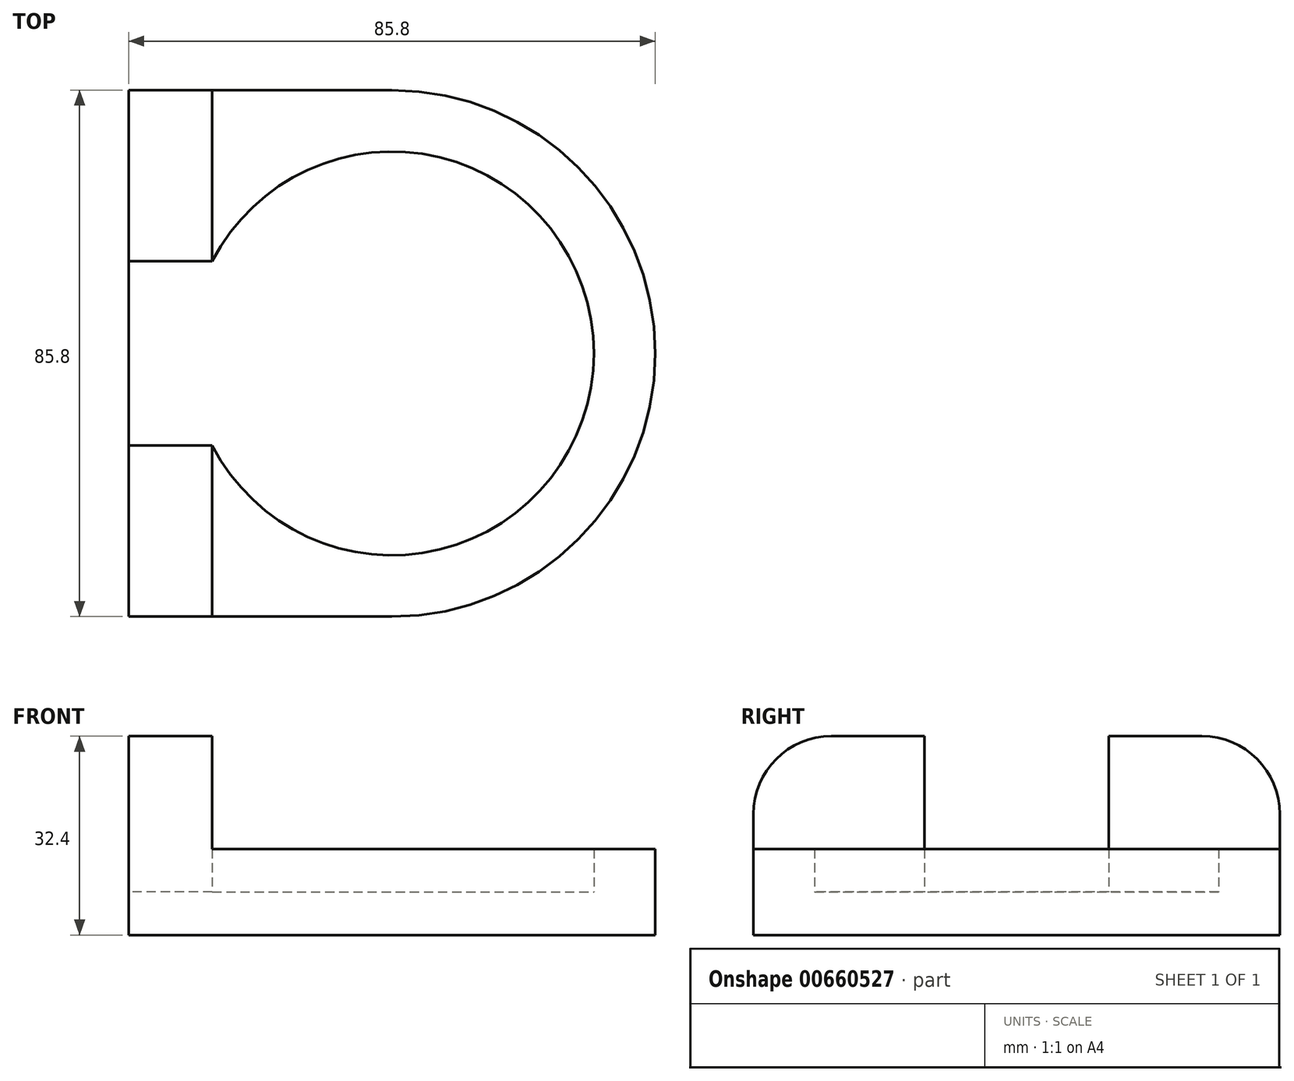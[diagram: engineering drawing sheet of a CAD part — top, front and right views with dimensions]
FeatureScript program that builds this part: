
annotation { "Feature Type Name" : "Feature", "Feature Type Description" : "" }
export const myFeature = defineFeature(function(context is Context, id is Id, definition is map)
    precondition{}
    {
        {
            var Q0;
            Q0=qCreatedBy(makeId("Top.planeOp"),FACE);
            var sketch = newSketch(context, id + "F0", { "sketchPlane" : qUnion([Q0])});
            skCircle(sketch, "E0", {"center": v(0, 0) * mm, "radius": 32.9 * mm});
            skCircle(sketch, "E1", {"center": v(0, 0) * mm, "radius": 42.9 * mm});
            skLineSegment(sketch, "E2", {"start": v(0, 42.9) * mm, "end": v(-42.9, 42.9) * mm});
            skLineSegment(sketch, "E3", {"start": v(-42.9, 42.9) * mm, "end": v(-42.9, -42.9) * mm});
            skLineSegment(sketch, "E4", {"start": v(-42.9, -42.9) * mm, "end": v(0, -42.9) * mm});
            skSolve(sketch);
        }
        {
            var Q0;
            {var subQ0=sQuery(id+"F0.wireOp",EDGE,"E2");Q0=makeQuery(id+"F0.imprint","IMPRINT",FACE,{"disambiguationData":[TD([[makeQuery(id+"F0.imprint","IMPRINT",EDGE,{"derivedFrom":subQ0}),1.0]])]});}
            var Q1;
            {var subQ0=sQuery(id+"F0.wireOp",EDGE,"E4");Q1=makeQuery(id+"F0.imprint","IMPRINT",FACE,{"disambiguationData":[TD([[makeQuery(id+"F0.imprint","IMPRINT",EDGE,{"derivedFrom":subQ0}),1.0]])]});}
            var Q2;
            Q2=makeQuery(id+"F0.imprint","IMPRINT",FACE,{"disambiguationData":[TD([[makeQuery(id+"F0.imprint","IMPRINT",EDGE,{"derivedFrom":sQuery(id+"F0.wireOp",EDGE,"E0")}),-1.0]])]});
            extrude(context, id + "F1", {"entities" : qUnion([Q0, Q1, Q2]), "depth" : 25.4 * mm, "offsetDistance" : 25.4 * mm});
        }
        {
            var Q0;
            Q0=qCreatedBy(makeId("Top.planeOp"),FACE);
            var sketch = newSketch(context, id + "F2", { "sketchPlane" : qUnion([Q0])});
            skCircle(sketch, "E5", {"center": v(0, 0) * mm, "radius": 32.9 * mm});
            skSolve(sketch);
        }
        {
            var Q0;
            Q0=makeQuery(id+"F1.opExtrude","CAP_FACE",FACE,{"disambiguationData":[OSD([sQuery(id+"F0.wireOp",EDGE,"E0"),sQuery(id+"F0.wireOp",EDGE,"E1"),sQuery(id+"F0.wireOp",EDGE,"E2"),sQuery(id+"F0.wireOp",EDGE,"E3"),sQuery(id+"F0.wireOp",EDGE,"E4")])],"isStart":true});
            var Q1;
            Q1=makeQuery(id+"F2.imprint","IMPRINT",FACE,{"disambiguationData":[TD([[makeQuery(id+"F2.imprint","IMPRINT",EDGE,{"derivedFrom":sQuery(id+"F2.wireOp",EDGE,"E5")}),1.0]])]});
            extrude(context, id + "F3", {"entities" : qUnion([Q0, Q1]), "operationType" : NewBodyOperationType.ADD, "depth" : 7 * mm, "offsetDistance" : 25.4 * mm});
        }
        {
            var Q0;
            Q0=qCreatedBy(makeId("Top.planeOp"),FACE);
            var sketch = newSketch(context, id + "F4", { "sketchPlane" : qUnion([Q0])});
            skLineSegment(sketch, "E6", {"start": v(-29.28, 15) * mm, "end": v(-42.9, 15) * mm});
            skLineSegment(sketch, "E7", {"start": v(-42.9, 15) * mm, "end": v(-42.9, -15) * mm});
            skLineSegment(sketch, "E8", {"start": v(-42.9, -15) * mm, "end": v(-29.28, -15) * mm});
            skArc(sketch, "E9", {"start": v(-29.28, 15) * mm, "mid": v(-32.9, 0) * mm, "end": v(-29.28, -15) * mm});
            skSolve(sketch);
        }
        {
            var Q0;
            Q0 = qSketchRegion(id + "F4", true);
            extrude(context, id + "F5", {"entities" : qUnion([Q0]), "operationType" : NewBodyOperationType.REMOVE, "depth" : 25.4 * mm, "offsetDistance" : 25.4 * mm});
        }
        {
            var Q0;
            Q0=makeQuery(id+"F1.opExtrude","CAP_FACE",FACE,{"disambiguationData":[OSD([sQuery(id+"F0.wireOp",EDGE,"E0"),sQuery(id+"F0.wireOp",EDGE,"E1"),sQuery(id+"F0.wireOp",EDGE,"E2"),sQuery(id+"F0.wireOp",EDGE,"E3"),sQuery(id+"F0.wireOp",EDGE,"E4")])],"isStart":false});
            var sketch = newSketch(context, id + "F6", { "sketchPlane" : qUnion([Q0])});
            skLineSegment(sketch, "E10", {"start": v(-29.28, 15) * mm, "end": v(-29.28, 42.9) * mm});
            skLineSegment(sketch, "E11", {"start": v(-29.28, 42.9) * mm, "end": v(0, 42.9) * mm});
            skLineSegment(sketch, "E12", {"start": v(0, -42.9) * mm, "end": v(-29.28, -42.9) * mm});
            skLineSegment(sketch, "E13", {"start": v(-29.28, -42.9) * mm, "end": v(-29.28, -15) * mm});
            skArc(sketch, "E14", {"start": v(-29.28, -15) * mm, "mid": v(32.9, 0) * mm, "end": v(-29.28, 15) * mm});
            skArc(sketch, "E15", {"start": v(0, -42.9) * mm, "mid": v(42.9, 0) * mm, "end": v(0, 42.9) * mm});
            skSolve(sketch);
        }
        {
            var Q0;
            Q0 = qSketchRegion(id + "F6", true);
            extrude(context, id + "F7", {"entities" : qUnion([Q0]), "operationType" : NewBodyOperationType.REMOVE, "oppositeDirection" : true, "depth" : 18.4 * mm, "offsetDistance" : 25.4 * mm});
        }
        {
            var Q0;
            Q0=makeQuery(id+"F1.opExtrude","CAP_EDGE",EDGE,{"disambiguationData":[OSD([sQuery(id+"F0.wireOp",EDGE,"E4")])],"isStart":false});
            var Q1;
            Q1=makeQuery(id+"F5.boolean.opBoolean","COPY",EDGE,{"derivedFrom":makeQuery(id+"F5.opExtrude","CAP_EDGE",EDGE,{"disambiguationData":[OSD([sQuery(id+"F4.wireOp",EDGE,"E8")])],"isStart":false})});
            var Q2;
            Q2=makeQuery(id+"F5.boolean.opBoolean","COPY",EDGE,{"derivedFrom":makeQuery(id+"F5.opExtrude","CAP_EDGE",EDGE,{"disambiguationData":[OSD([sQuery(id+"F4.wireOp",EDGE,"E6")])],"isStart":false})});
            var Q3;
            Q3=makeQuery(id+"F1.opExtrude","CAP_EDGE",EDGE,{"disambiguationData":[OSD([sQuery(id+"F0.wireOp",EDGE,"E2")])],"isStart":false});
            fillet(context, id + "F8", {"entities" : qUnion([Q0, Q1, Q2, Q3]), "radius" : 12.7 * mm, "tangentPropagation" : true, "allowEdgeOverflow" : false});
        }
    });
